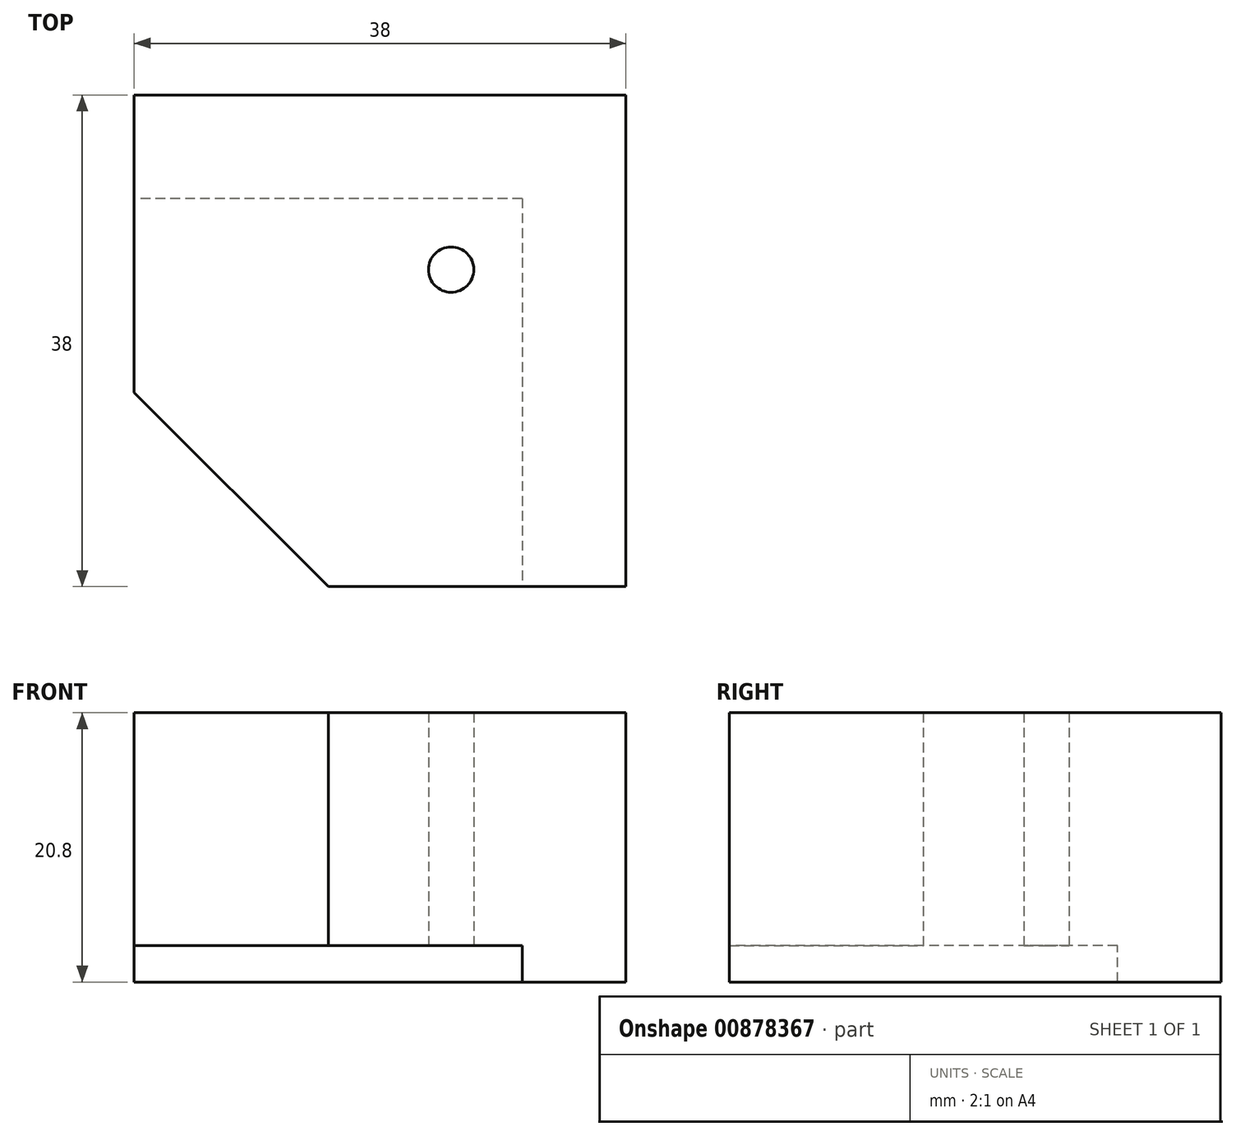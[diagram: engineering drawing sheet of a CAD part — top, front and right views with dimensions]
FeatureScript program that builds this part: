
annotation { "Feature Type Name" : "Feature", "Feature Type Description" : "" }
export const myFeature = defineFeature(function(context is Context, id is Id, definition is map)
    precondition{}
    {
        {
            var Q0;
            Q0=qCreatedBy(makeId("Top.planeOp"),FACE);
            var sketch = newSketch(context, id + "F0", { "sketchPlane" : qUnion([Q0])});
            skCircle(sketch, "E0", {"center": v(0, 0) * mm, "radius": 1.75 * mm});
            skCircle(sketch, "E1", {"center": v(0, 0) * mm, "radius": 5.5 * mm, "construction": true});
            skLineSegment(sketch, "E2", {"start": v(5.5, 0) * mm, "end": v(5.5, -24.5) * mm});
            skLineSegment(sketch, "E3", {"start": v(0, 5.5) * mm, "end": v(-24.5, 5.5) * mm});
            skLineSegment(sketch, "E4", {"start": v(-24.5, 5.5) * mm, "end": v(-24.5, -9.5) * mm});
            skLineSegment(sketch, "E5", {"start": v(5.5, -24.5) * mm, "end": v(-9.5, -24.5) * mm});
            skLineSegment(sketch, "E6", {"start": v(-9.5, -24.5) * mm, "end": v(-24.5, -9.5) * mm});
            skLineSegment(sketch, "E7", {"start": v(0, 5.5) * mm, "end": v(5.5, 5.5) * mm});
            skLineSegment(sketch, "E8", {"start": v(5.5, 5.5) * mm, "end": v(5.5, 0) * mm});
            skLineSegment(sketch, "E9.0", {"start": v(0, 13.5) * mm, "end": v(-24.5, 13.5) * mm});
            skLineSegment(sketch, "E9.1", {"start": v(0, 13.5) * mm, "end": v(13.5, 13.5) * mm});
            skLineSegment(sketch, "E9.2", {"start": v(13.5, 13.5) * mm, "end": v(13.5, 0) * mm});
            skLineSegment(sketch, "E9.3", {"start": v(13.5, 0) * mm, "end": v(13.5, -24.5) * mm});
            skLineSegment(sketch, "E10", {"start": v(-24.5, 13.5) * mm, "end": v(-24.5, 5.5) * mm});
            skLineSegment(sketch, "E11", {"start": v(5.5, -24.5) * mm, "end": v(13.5, -24.5) * mm});
            skSolve(sketch);
        }
        {
            var Q0;
            Q0=makeQuery(id+"F0.imprint","IMPRINT",FACE,{"disambiguationData":[TD([[makeQuery(id+"F0.imprint","IMPRINT",EDGE,{"derivedFrom":sQuery(id+"F0.wireOp",EDGE,"E0")}),-1.0]])]});
            var Q1;
            Q1=makeQuery(id+"F0.imprint","IMPRINT",FACE,{"disambiguationData":[TD([[makeQuery(id+"F0.imprint","IMPRINT",EDGE,{"derivedFrom":sQuery(id+"F0.wireOp",EDGE,"E2")}),1.0]])]});
            extrude(context, id + "F1", {"entities" : qUnion([Q0, Q1]), "depth" : 18 * mm, "offsetDistance" : 25 * mm});
        }
        {
            var Q0;
            Q0=makeQuery(id+"F0.imprint","IMPRINT",FACE,{"disambiguationData":[TD([[makeQuery(id+"F0.imprint","IMPRINT",EDGE,{"derivedFrom":sQuery(id+"F0.wireOp",EDGE,"E2")}),1.0]])]});
            extrude(context, id + "F2", {"entities" : qUnion([Q0]), "operationType" : NewBodyOperationType.ADD, "oppositeDirection" : true, "depth" : 2.8 * mm, "offsetDistance" : 25 * mm});
        }
    });
